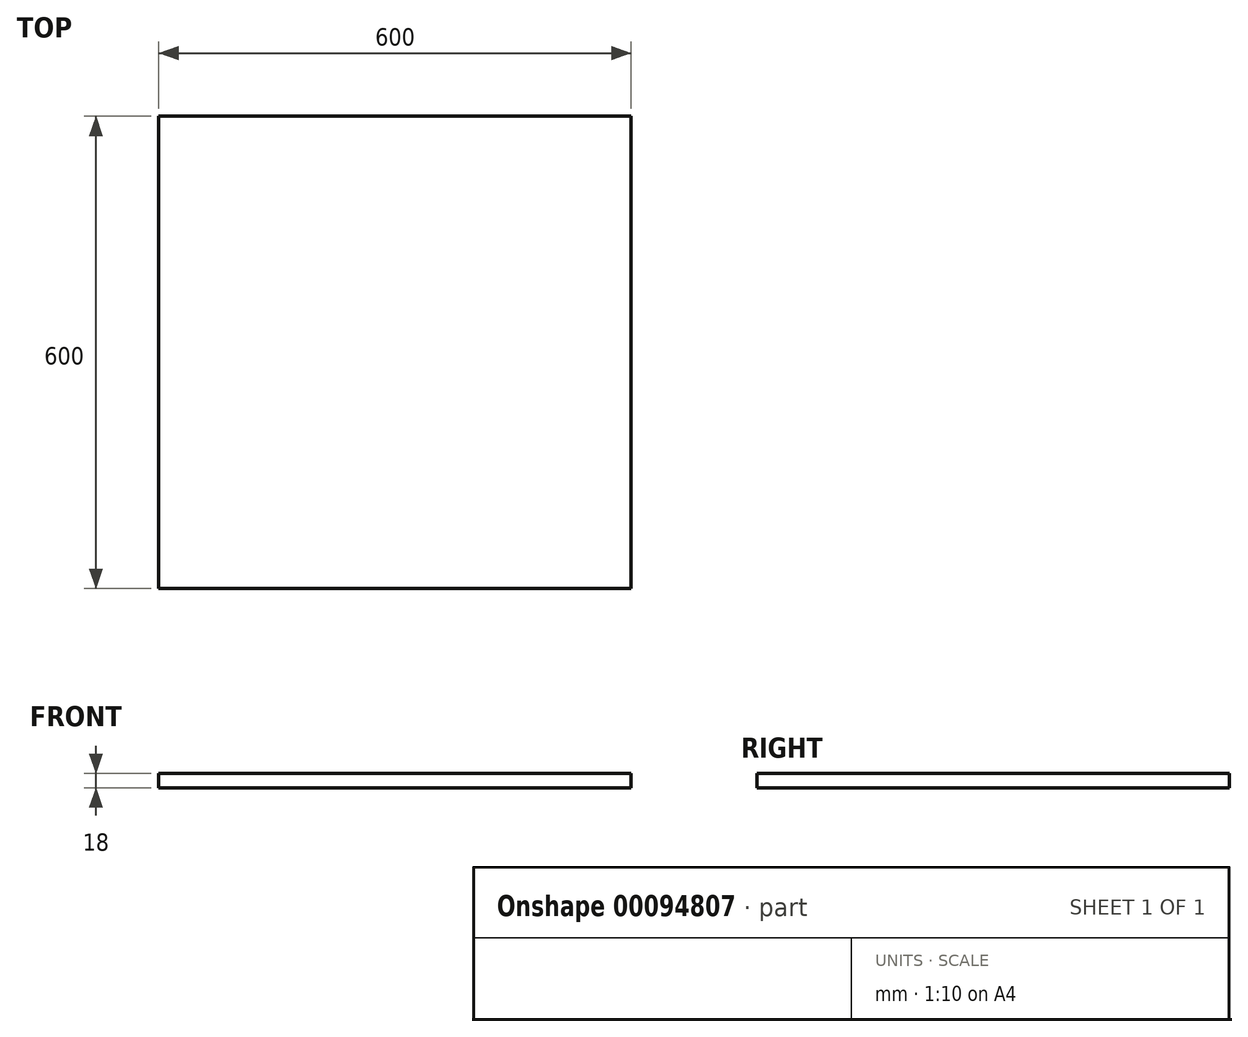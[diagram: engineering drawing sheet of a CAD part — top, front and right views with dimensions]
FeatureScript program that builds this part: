
annotation { "Feature Type Name" : "Feature", "Feature Type Description" : "" }
export const myFeature = defineFeature(function(context is Context, id is Id, definition is map)
    precondition{}
    {
        {
            var Q0;
            Q0=qCreatedBy(makeId("Top.planeOp"),FACE);
            var sketch = newSketch(context, id + "F0", { "sketchPlane" : qUnion([Q0])});
            skLineSegment(sketch, "E0.bottom", {"start": v(-251.44, 333.39) * mm, "end": v(348.56, 333.39) * mm});
            skLineSegment(sketch, "E0.top", {"start": v(-251.44, -266.61) * mm, "end": v(348.56, -266.61) * mm});
            skLineSegment(sketch, "E0.left", {"start": v(-251.44, 333.39) * mm, "end": v(-251.44, -266.61) * mm});
            skLineSegment(sketch, "E0.right", {"start": v(348.56, 333.39) * mm, "end": v(348.56, -266.61) * mm});
            skSolve(sketch);
        }
        {
            var Q0;
            Q0=makeQuery(id+"F0.imprint","IMPRINT",FACE,{"disambiguationData":[TD([[makeQuery(id+"F0.imprint","IMPRINT",EDGE,{"derivedFrom":sQuery(id+"F0.wireOp",EDGE,"E0.bottom")}),-1.0]])]});
            extrude(context, id + "F1", {"entities" : qUnion([Q0]), "depth" : 18 * mm});
        }
    });
